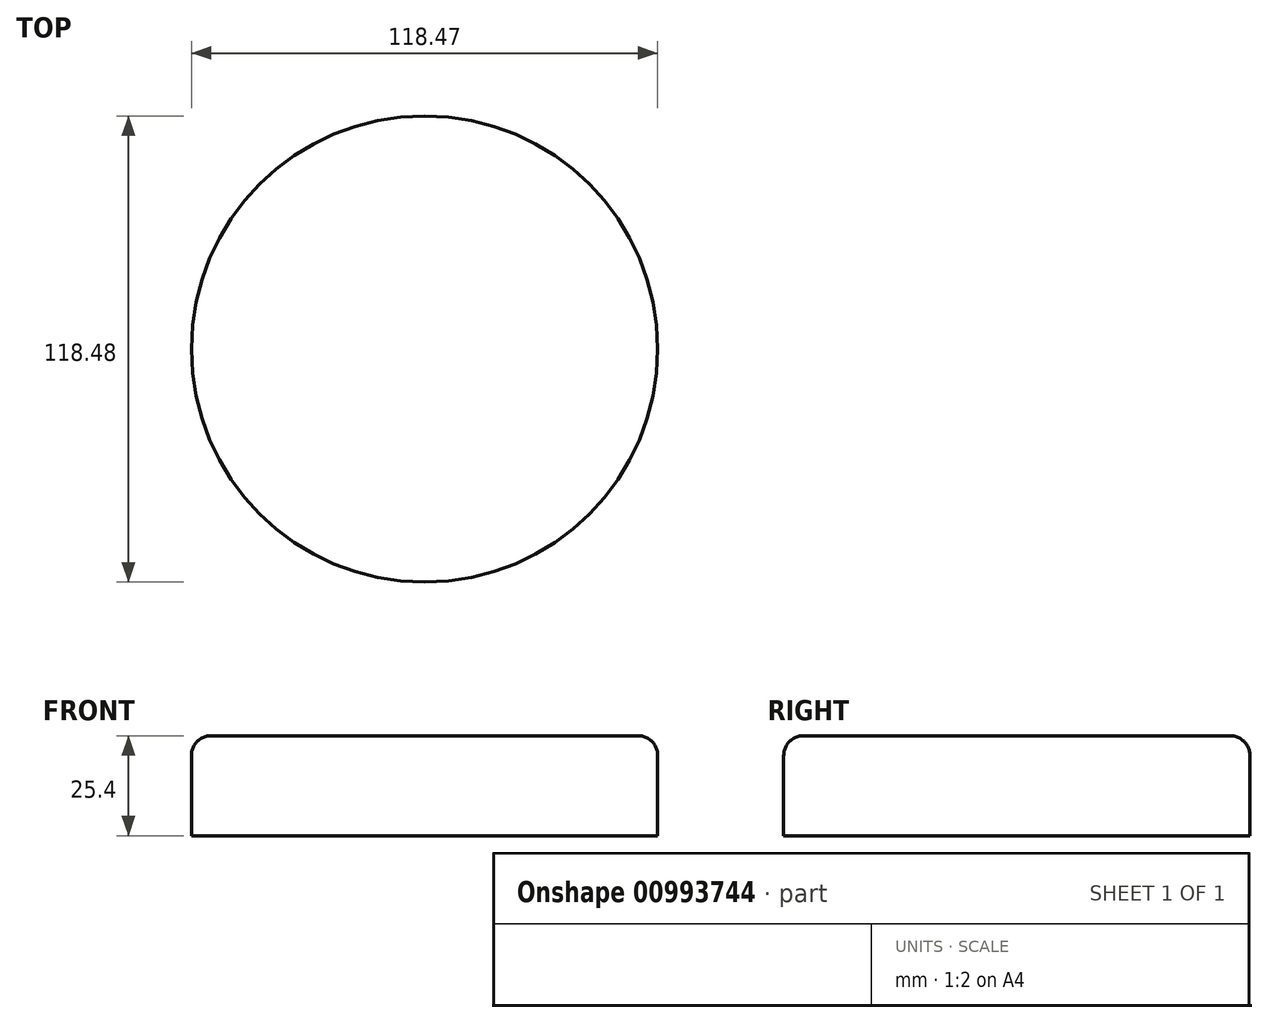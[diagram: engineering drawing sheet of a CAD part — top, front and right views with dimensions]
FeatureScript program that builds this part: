
annotation { "Feature Type Name" : "Feature", "Feature Type Description" : "" }
export const myFeature = defineFeature(function(context is Context, id is Id, definition is map)
    precondition{}
    {
        {
            var Q0;
            Q0=qCreatedBy(makeId("Top.planeOp"),FACE);
            var sketch = newSketch(context, id + "F0", { "sketchPlane" : qUnion([Q0])});
            skCircle(sketch, "E0", {"center": v(-124.24, 9.32) * mm, "radius": 59.24 * mm});
            skSolve(sketch);
        }
        {
            var Q0;
            Q0 = qSketchRegion(id + "FIH5hNrdZuc63p5_0", true);
            var Q1;
            Q1=makeQuery(id+"F0.imprint","IMPRINT",FACE,{"disambiguationData":[TD([[makeQuery(id+"F0.imprint","IMPRINT",EDGE,{"derivedFrom":sQuery(id+"F0.wireOp",EDGE,"E0")}),1.0]])]});
            extrude(context, id + "F1", {"entities" : qUnion([Q0, Q1]), "depth" : 25.4 * mm, "offsetDistance" : 25.4 * mm});
        }
        {
            var Q0;
            Q0=makeQuery(id+"F1.opExtrude","CAP_EDGE",EDGE,{"disambiguationData":[OSD([sQuery(id+"F0.wireOp",EDGE,"E0")])],"isStart":false});
            fillet(context, id + "F2", {"entities" : qUnion([Q0]), "radius" : 5.08 * mm, "tangentPropagation" : true, "allowEdgeOverflow" : false});
        }
    });
